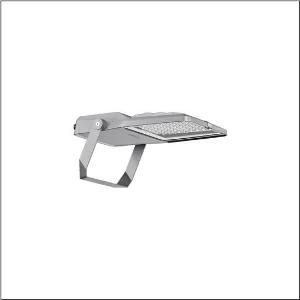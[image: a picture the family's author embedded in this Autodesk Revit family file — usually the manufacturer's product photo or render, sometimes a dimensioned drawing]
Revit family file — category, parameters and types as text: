
# Revit family: floodlight_fl_21_iq_mini___pl33t_5xa7771b4f1a_48a0
name_source: partatom
category: Lighting Fixtures
units: mm (PartAtom-declared; Revit-internal decimal feet)

## family parameters
Cut with Voids When Loaded = No
Host = Face
Light Source = No
Part Type = Normal
Room Calculation Point = No
Round Connector Dimension = Use Diameter
Shared = No

## types (1)
- --- (1 x LED, 6420 lm, 45.5 W, 4000K)
    Apparent Load = 46 VA
    CIE Flux Codes = 26 75 99 100 100
    Color Rendering = 70
    Color Temperature = 4000K
    Default Elevation = 1800 mm
    Description = Floodlight FL 21 iQ mini, floodlight, primary light control with lens, of PMMA, primary optical cover: protective disc, of toughened safety glass, transparent, light distribution: PL33T, light emission: direct distribution, installation type: surface-mounted, LED, High Power LED, rated luminous flux: 6.420lm, luminous efficacy: 141lm/W, light colour: 740, colour temperature: 4000K, control: Auto-Match, Temp-Guard, Lumen-Switch, Night-Set, Smart-Wire, Light-Fading, Desk-Remote (wireless, voltage-free reading and setting of iQ features in the workshop via application-optimized NFC function/RFID function), optimised constant luminous flux control (CLO 2.0), with terminal, 6-pole, mains connection: 220..240V, AC, 50/60Hz, start of lifetime: 46W, end of service life: 48W, reduction: 22W, luminaire housing, of diecast aluminium, powder-coated, Siteco® metallic grey (DB 702S), corrosivity category C5 mid according to DIN EN ISO 12944, sealing non-destructively replaceable, mounting bracket, of steel, galvanised, powder-coated, Siteco® metallic grey (DB 702S), protection rating (complete): IP66, insulation class (complete): insulation class II (safety insulation), certification: CE, ENEC, VDE, protection symbol: D, impact resistance: IK08, permissible operating ambient temperature: -40..+40°C, permissible operating ambient temperature for outdoor applications: -40..+50°C, standard: DIN EN 12944, LABS conformity tested according to VDMA 24364:2018-05, packaging unit: 1 piece

Light Distribution: PL33T
    Height = 70 mm
    Lamp = 1 x LED
    Lamp Light Flux = 6420 lm
    Lamp Power = 45.5 W
    Lamp count = 1
    Length = 485 mm
    Luminous efficacy = 141 lm/W
    Manufacturer = Siteco
    ModVariant = No
    Model = 5XA7771B4F1A
    Mounting Place = Wall
    Mounting Type = Surface mounted
    Number of Poles = 1
    OnlyDefault = Yes
    Power Factor = 1
    Product Name = Floodlight FL 21 iQ mini | PL33T
    Product group = floodlight | wall mounted
    ProductGroupID = 2001
    Protection Class = Protection class II
    Protection Degree = IP 66
    RLX_Detail_Level = 1
    RLX_Emergency_Light_Flux = 0 lm
    RLX_Emergency_Type = 0
    RLX_Emergency_Type_DB = No
    RlxData = <blob elided: 96041 chars, md5=10f442fe>
    Socket = socket
    Standby Power = 0 W
    System Light Flux = 6420 lm
    System Power = 46 W
    Type Comments = factory setting: luminous flux: 100 % | dim-lin: 254 | 463 mA
    Type Image = l_1006845.jpg
    URL = http://relux.com
    VarID = @adj_100405
    Voltage = 0 V
    Weight = 0.00 kg
    Width = 337 mm

## geometry (parser evidence)
native form markers: Blend x4, Sweep x12
no freeform markers — native parametric forms only
